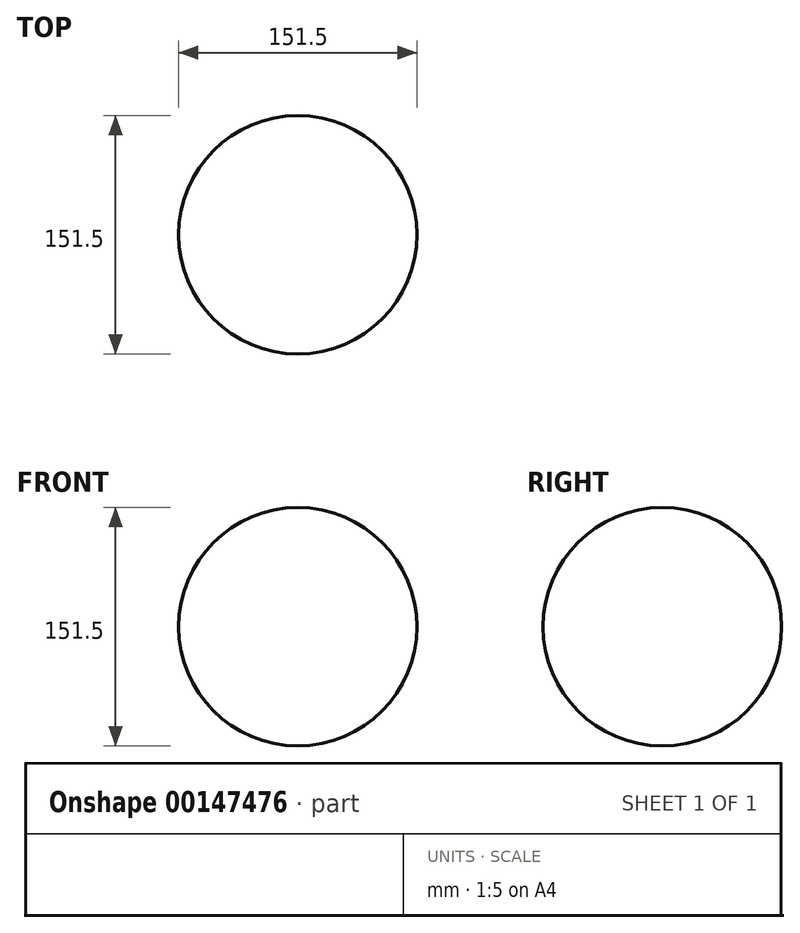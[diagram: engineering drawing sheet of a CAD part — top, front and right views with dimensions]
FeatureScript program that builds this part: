
annotation { "Feature Type Name" : "Feature", "Feature Type Description" : "" }
export const myFeature = defineFeature(function(context is Context, id is Id, definition is map)
    precondition{}
    {
        {
            var Q0;
            Q0=qCreatedBy(makeId("Front.planeOp"),FACE);
            var sketch = newSketch(context, id + "F0", { "sketchPlane" : qUnion([Q0])});
            skCircle(sketch, "E0", {"center": v(0, 0) * mm, "radius": 75.75 * mm});
            skLineSegment(sketch, "E1", {"start": v(0, 75.75) * mm, "end": v(0, -75.75) * mm});
            skSolve(sketch);
        }
        {
            var Q0;
            {var subQ0=sQuery(id+"F0.wireOp",EDGE,"E1");Q0=makeQuery(id+"F0.imprint","IMPRINT",FACE,{"disambiguationData":[TD([[makeQuery(id+"F0.imprint","IMPRINT",EDGE,{"derivedFrom":subQ0}),-1.0]])]});}
            var Q1;
            Q1=sQuery(id+"F0.wireOp",EDGE,"E1");
            revolve(context, id + "F1", {"entities" : qUnion([Q0]), "axis" : qUnion([Q1]), "revolveType" : RevolveType.FULL});
        }
    });
